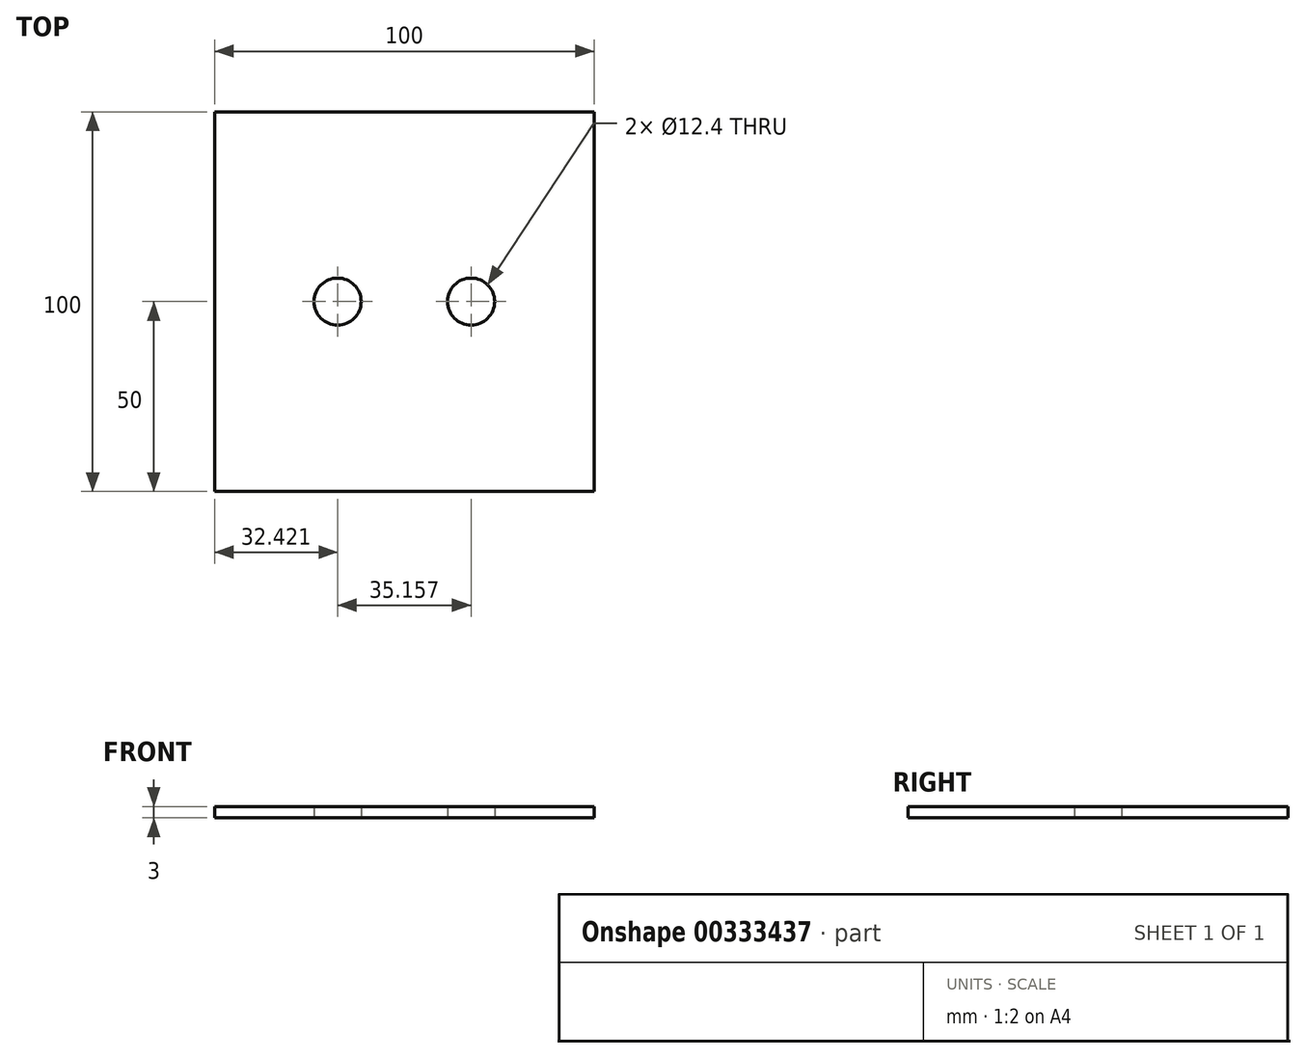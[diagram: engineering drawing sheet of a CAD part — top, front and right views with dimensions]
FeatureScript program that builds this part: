
annotation { "Feature Type Name" : "Feature", "Feature Type Description" : "" }
export const myFeature = defineFeature(function(context is Context, id is Id, definition is map)
    precondition{}
    {
        {
            var Q0;
            Q0=qCreatedBy(makeId("Top.planeOp"),FACE);
            var sketch = newSketch(context, id + "F0", { "sketchPlane" : qUnion([Q0])});
            skLineSegment(sketch, "E0.bottom", {"start": v(0, 0) * mm, "end": v(100, 0) * mm});
            skLineSegment(sketch, "E0.top", {"start": v(0, 100) * mm, "end": v(100, 100) * mm});
            skLineSegment(sketch, "E0.left", {"start": v(0, 0) * mm, "end": v(0, 100) * mm});
            skLineSegment(sketch, "E0.right", {"start": v(100, 0) * mm, "end": v(100, 100) * mm});
            skLineSegment(sketch, "E1.bottom", {"start": v(0, 0) * mm, "end": v(50, 0) * mm});
            skLineSegment(sketch, "E1.left", {"start": v(0, 0) * mm, "end": v(0, 50) * mm});
            skLineSegment(sketch, "E1.right", {"start": v(50, 0) * mm, "end": v(50, 50) * mm});
            skLineSegment(sketch, "E2", {"start": v(50, 50) * mm, "end": v(67.58, 50) * mm});
            skLineSegment(sketch, "E3", {"start": v(50, 50) * mm, "end": v(32.42, 50) * mm});
            skCircle(sketch, "E4", {"center": v(67.58, 50) * mm, "radius": 6.2 * mm});
            skCircle(sketch, "E5", {"center": v(32.42, 50) * mm, "radius": 6.2 * mm});
            skSolve(sketch);
        }
        {
            var Q0;
            Q0=makeQuery(id+"F0.imprint","IMPRINT",FACE,{"disambiguationData":[TD([[makeQuery(id+"F0.imprint","IMPRINT",EDGE,{"derivedFrom":sQuery(id+"F0.wireOp",EDGE,"E0.bottom")}),1.0]])]});
            extrude(context, id + "F1", {"entities" : qUnion([Q0]), "depth" : 3 * mm});
        }
    });
